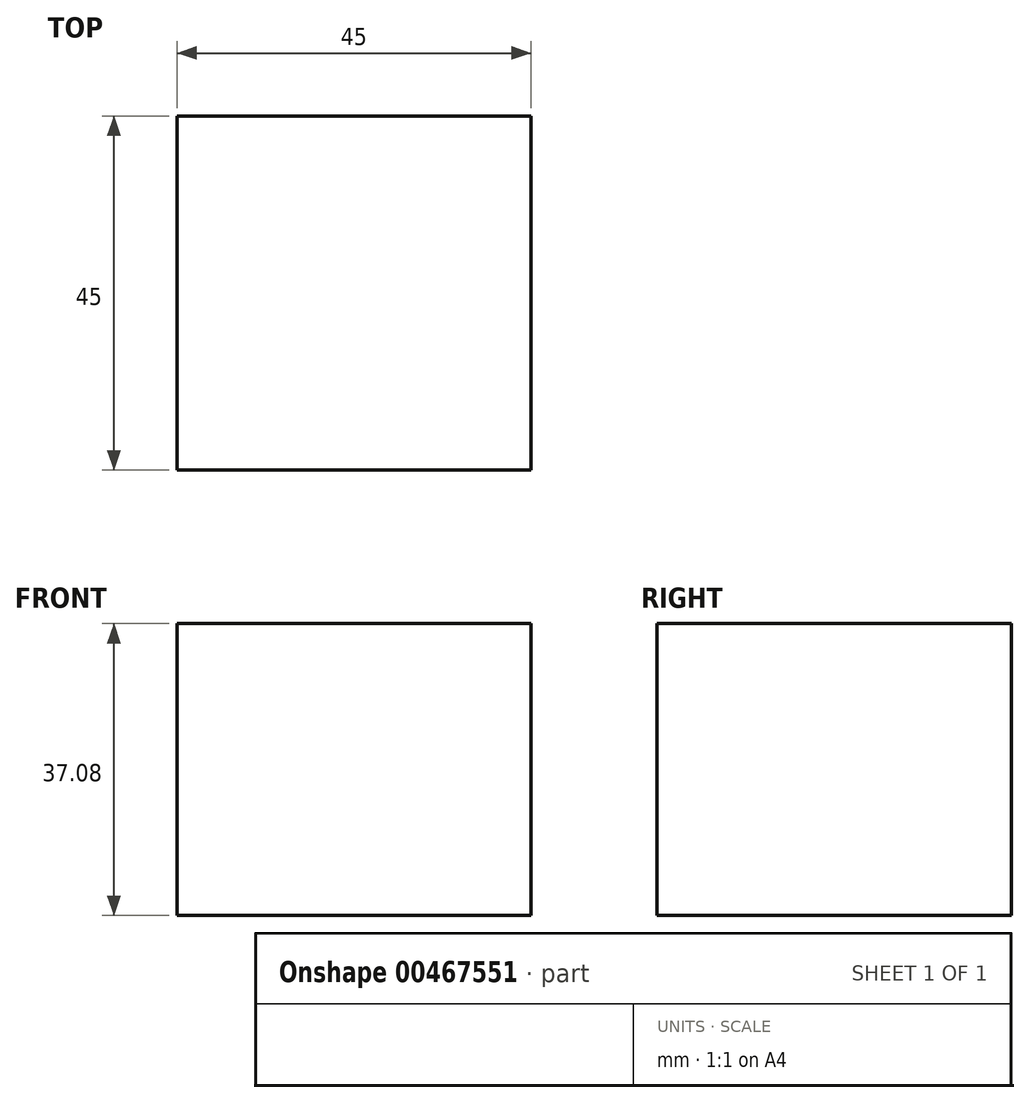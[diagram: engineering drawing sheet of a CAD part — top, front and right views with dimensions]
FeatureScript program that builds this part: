
annotation { "Feature Type Name" : "Feature", "Feature Type Description" : "" }
export const myFeature = defineFeature(function(context is Context, id is Id, definition is map)
    precondition{}
    {
        {
            var Q0;
            Q0=qCreatedBy(makeId("Top.planeOp"),FACE);
            var sketch = newSketch(context, id + "F0", { "sketchPlane" : qUnion([Q0])});
            skLineSegment(sketch, "E0.bottom", {"start": v(0, 0) * mm, "end": v(45, 0) * mm});
            skLineSegment(sketch, "E0.top", {"start": v(0, 45) * mm, "end": v(45, 45) * mm});
            skLineSegment(sketch, "E0.left", {"start": v(0, 0) * mm, "end": v(0, 45) * mm});
            skLineSegment(sketch, "E0.right", {"start": v(45, 0) * mm, "end": v(45, 45) * mm});
            skSolve(sketch);
        }
        {
            var Q0;
            Q0=qSketchRegion(id+"F0",true);
            extrude(context, id + "F1", {"entities" : qUnion([Q0]), "depth" : 18 * 2.06 * mm});
        }
    });
